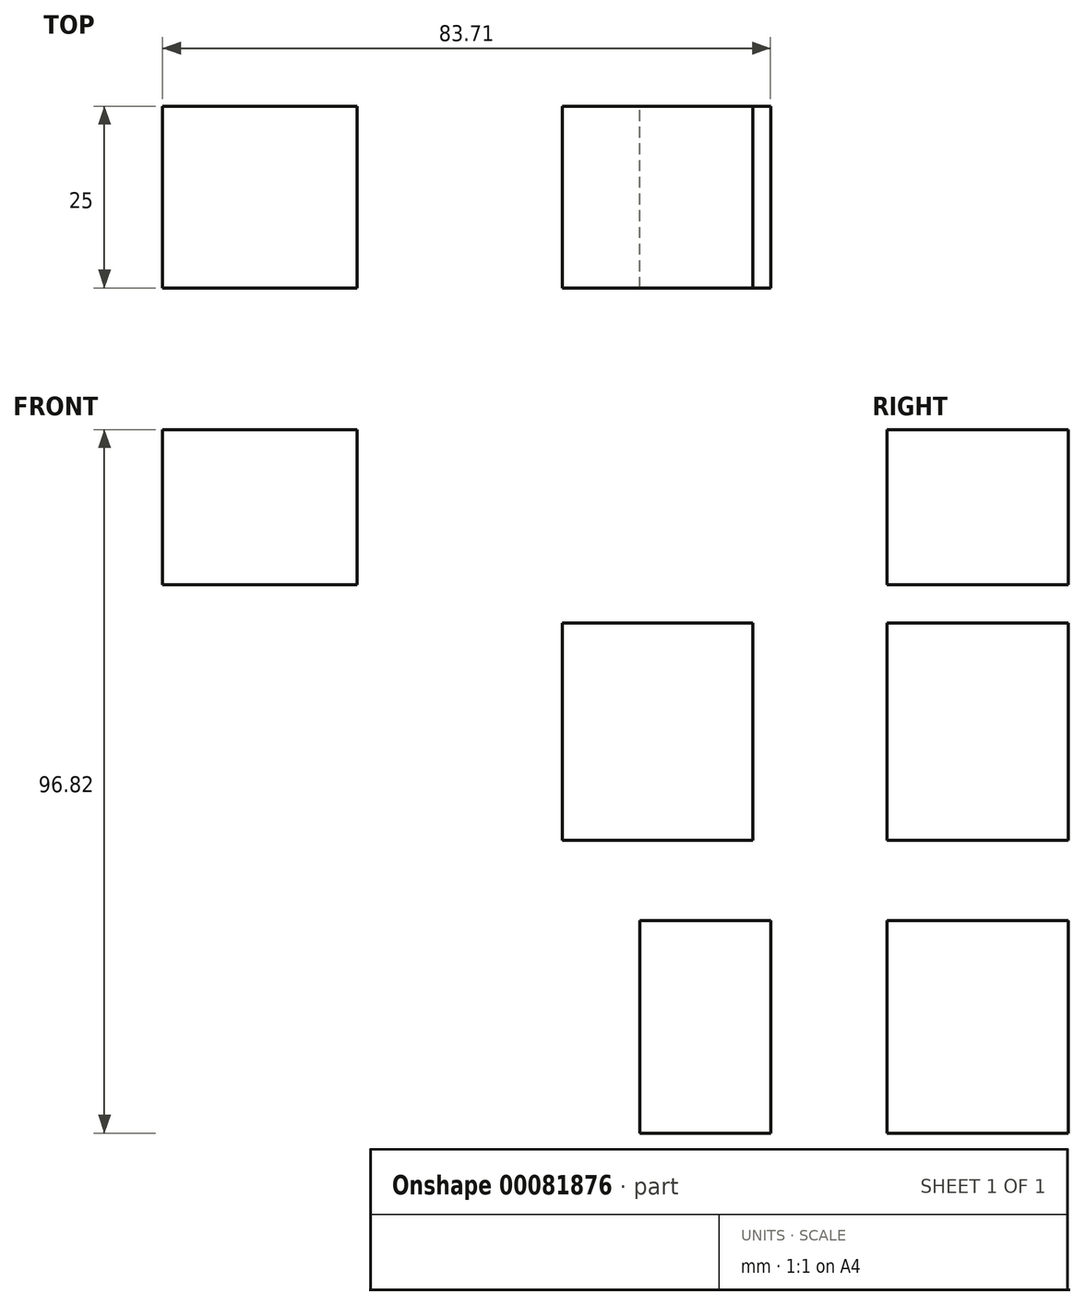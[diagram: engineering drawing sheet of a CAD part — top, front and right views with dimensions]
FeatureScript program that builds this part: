
annotation { "Feature Type Name" : "Feature", "Feature Type Description" : "" }
export const myFeature = defineFeature(function(context is Context, id is Id, definition is map)
    precondition{}
    {
        {
            var Q0;
            Q0=qCreatedBy(makeId("Front.planeOp"),FACE);
            var sketch = newSketch(context, id + "F0", { "sketchPlane" : qUnion([Q0])});
            skLineSegment(sketch, "E0.bottom", {"start": v(-93.45, 57.77) * mm, "end": v(-66.67, 57.77) * mm});
            skLineSegment(sketch, "E0.top", {"start": v(-93.45, 36.43) * mm, "end": v(-66.67, 36.43) * mm});
            skLineSegment(sketch, "E0.left", {"start": v(-93.45, 57.77) * mm, "end": v(-93.45, 36.43) * mm});
            skLineSegment(sketch, "E0.right", {"start": v(-66.67, 57.77) * mm, "end": v(-66.67, 36.43) * mm});
            skLineSegment(sketch, "E1.bottom", {"start": v(-38.4, 31.18) * mm, "end": v(-12.17, 31.18) * mm});
            skLineSegment(sketch, "E1.top", {"start": v(-38.4, 1.22) * mm, "end": v(-12.17, 1.22) * mm});
            skLineSegment(sketch, "E1.left", {"start": v(-38.4, 31.18) * mm, "end": v(-38.4, 1.22) * mm});
            skLineSegment(sketch, "E1.right", {"start": v(-12.17, 31.18) * mm, "end": v(-12.17, 1.22) * mm});
            skLineSegment(sketch, "E2.bottom", {"start": v(-27.72, -9.83) * mm, "end": v(-9.74, -9.83) * mm});
            skLineSegment(sketch, "E2.top", {"start": v(-27.72, -39.05) * mm, "end": v(-9.74, -39.05) * mm});
            skLineSegment(sketch, "E2.left", {"start": v(-27.72, -9.83) * mm, "end": v(-27.72, -39.05) * mm});
            skLineSegment(sketch, "E2.right", {"start": v(-9.74, -9.83) * mm, "end": v(-9.74, -39.05) * mm});
            skSolve(sketch);
        }
        {
            var Q0;
            Q0 = qSketchRegion(id + "F0", true);
            extrude(context, id + "F1", {"entities" : qUnion([Q0]), "depth" : 25 * mm});
        }
    });
